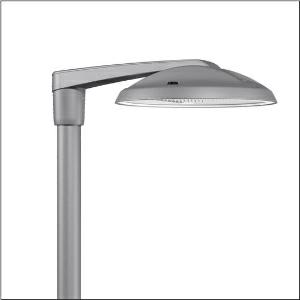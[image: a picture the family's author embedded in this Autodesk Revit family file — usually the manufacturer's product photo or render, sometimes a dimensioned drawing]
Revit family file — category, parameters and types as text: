
# Revit family: dl_r__50_iq_mini___st1_0a_5xa248d31v08ne_16c2
name_source: partatom
category: Lighting Fixtures
units: mm (PartAtom-declared; Revit-internal decimal feet)

## family parameters
Cut with Voids When Loaded = No
Host = Face
Light Source = No
Part Type = Normal
Room Calculation Point = No
Round Connector Dimension = Use Diameter
Shared = No

## types (1)
- --- (1 x LED, 17900 lm, 110.1 W, 3000K)
    Apparent Load = 110 VA
    CIE Flux Codes = 37 72 97 100 100
    Color Rendering = 70
    Color Temperature = 3000K
    Default Elevation = 1800 mm
    Description = DL® 50 iQ mini, mast luminaire, primary light control with lens, of PMMA, primary optical cover: cover, of toughened safety glass, transparent, light distribution: ST1.0a, light emission: direct distribution, primary light characteristic: asymmetric, installation type: post-top, side-entry, LED, High Power LED, rated luminous flux: 17.900lm, luminous efficacy: 163lm/W, light colour: 730, colour temperature: 3000K, control: optimised constant luminous flux control (CLO 2.0), Desk-Remote (wireless, voltage-free reading and setting of iQ features in the workshop via application-optimized NFC function/RFID function), Light-Fading, Smart-Wire, Night-Set, Lumen-Switch, Temp-Guard, Auto-Match, Street-Remote, pre-setting: logarithmic dimming characteristic, mains connection: 230..240V, AC, 50/60Hz, connection cable pre-assembled, cable length: 10,5m, start of lifetime: 110W, end of service life: 116W, reduction: 50W, luminaire housing, of diecast aluminium, powder-coated, Siteco® metallic grey (DB 702S), inclination adjustable: 0°, 5°, 10° (post-top) | 0°, -5°, -10°, -15° (side-entry), please order mast post-top element or mast side-entry element separately, diameter: 500mm, height: 115mm, post-top: for spigot size d x l = 76 x 100mm; with reducer (optional accessory) 60 x 100mm | side-entry: for spigot size d x l = 60 x 100mm; with reducer (optional accessory) 42 x 100mm, Smart Interface above, protection rating (complete): IP66, insulation class (complete): insulation class II (safety insulation), certification: CE, ENEC, ENEC+, VDE, impact resistance: IK08, permissible operating ambient temperature for outdoor applications: -25..+40°C, standard-compliant lighting for roads and squares, packaging unit: 1 piece

Light Distribution: ST1.0a
    Height = 115 mm
    Lamp = 1 x LED
    Lamp Light Flux = 17900 lm
    Lamp Power = 110.1 W
    Lamp count = 1
    Length = 500 mm
    Luminous efficacy = 163 lm/W
    Manufacturer = Siteco
    ModVariant = No
    Model = 5XA248D31V08NE
    Number of Poles = 1
    OnlyDefault = Yes
    Power Factor = 1
    Product Name = DL® 50 iQ mini | ST1.0a
    Product group = mast luminaire | pylon top
    ProductGroupID = 6100
    Protection Class = Protection class II
    Protection Degree = IP 66
    RLX_Detail_Level = 1
    RLX_Emergency_Light_Flux = 0 lm
    RLX_Emergency_Type = 0
    RLX_Emergency_Type_DB = No
    RlxData = <blob elided: 106965 chars, md5=5c097f63>
    Socket = socket
    Standby Power = 0 W
    System Light Flux = 17900 lm
    System Power = 110 W
    Type Comments = factory setting: luminous flux: 100 % | dim-lin: 254 | 601 mA
    Type Image = l_1251788.jpg
    URL = http://relux.com
    VarID = @adj_033471
    Voltage = 0 V
    Weight = 0.00 kg
    Width = 0 mm  [stored 0 ft]

note: [stored X ft] marks values corroborated as IEEE doubles in the binary element streams (Revit-internal decimal feet)

## geometry (parser evidence)
native form markers: Blend x4, Sweep x9
no freeform markers — native parametric forms only
